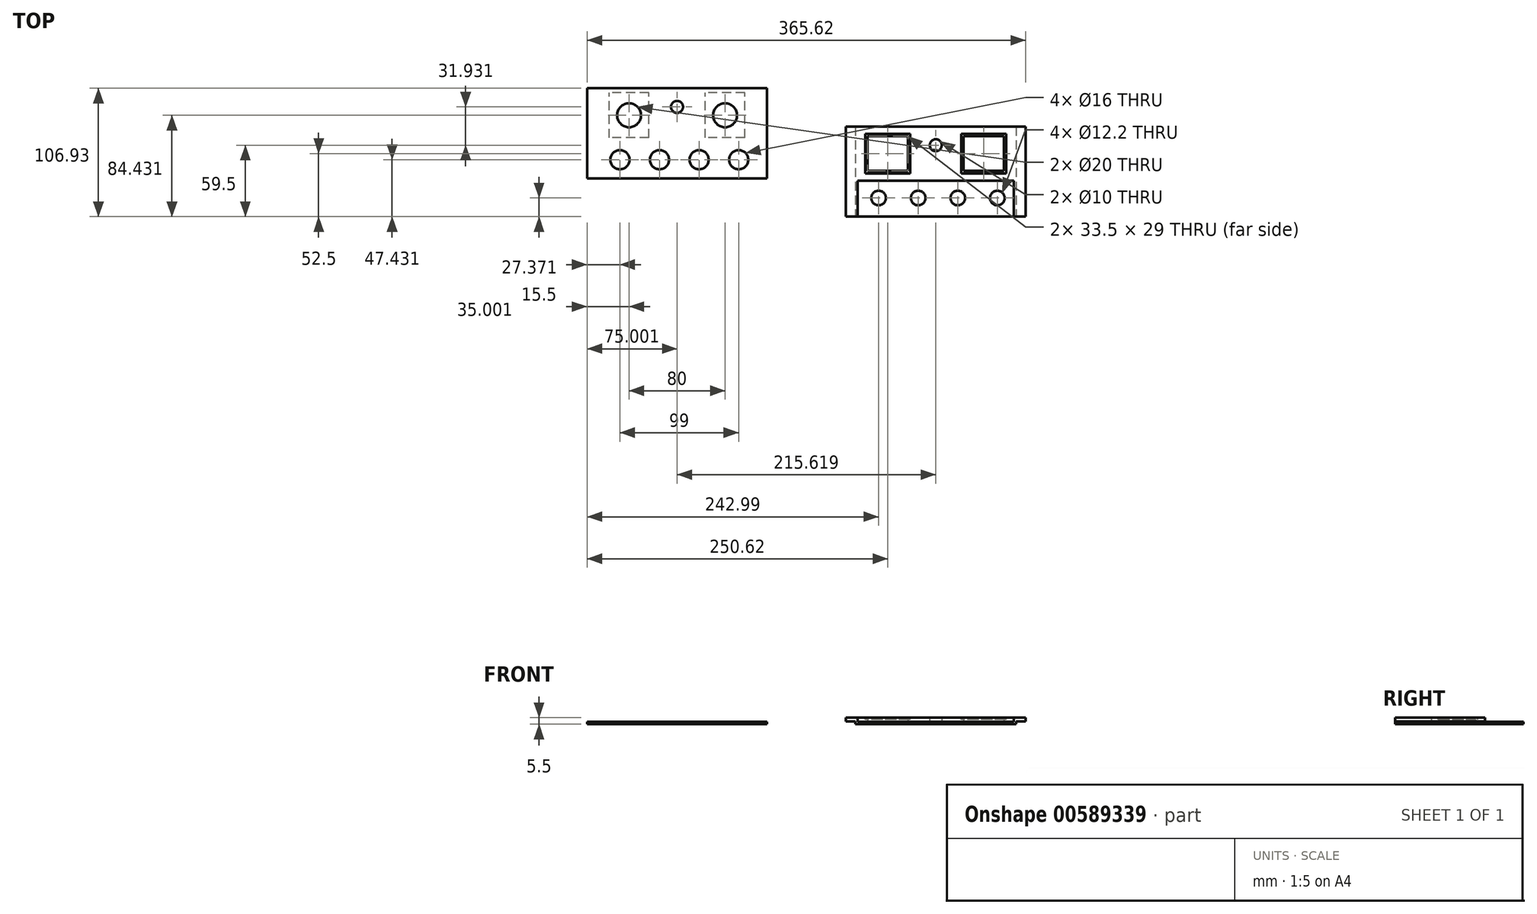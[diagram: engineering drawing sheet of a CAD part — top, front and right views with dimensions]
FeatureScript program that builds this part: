
annotation { "Feature Type Name" : "Feature", "Feature Type Description" : "" }
export const myFeature = defineFeature(function(context is Context, id is Id, definition is map)
    precondition{}
    {
        {
            var Q0;
            Q0=qCreatedBy(makeId("Top.planeOp"),FACE);
            var sketch = newSketch(context, id + "F0", { "sketchPlane" : qUnion([Q0])});
            skLineSegment(sketch, "E0.bottom", {"start": v(75, -37.5) * mm, "end": v(-75, -37.5) * mm});
            skLineSegment(sketch, "E0.top", {"start": v(75, 37.5) * mm, "end": v(-75, 37.5) * mm});
            skLineSegment(sketch, "E0.left", {"start": v(75, -37.5) * mm, "end": v(75, 37.5) * mm});
            skLineSegment(sketch, "E0.right", {"start": v(-75, -37.5) * mm, "end": v(-75, 37.5) * mm});
            skPoint(sketch, "E0.middle", {"position": v(0, 0) * mm});
            skCircle(sketch, "E1", {"center": v(0, 22) * mm, "radius": 5 * mm});
            skCircle(sketch, "E2", {"center": v(-47.63, -22) * mm, "radius": 6.1 * mm});
            skCircle(sketch, "E3.1.0.0", {"center": v(-14.63, -22) * mm, "radius": 6.1 * mm});
            skCircle(sketch, "E3.2.0.0", {"center": v(18.37, -22) * mm, "radius": 6.1 * mm});
            skCircle(sketch, "E3.3.0.0", {"center": v(51.37, -22) * mm, "radius": 6.1 * mm});
            skLineSegment(sketch, "E3.direction1", {"start": v(-47.63, -22) * mm, "end": v(-14.63, -22) * mm, "construction": true});
            skLineSegment(sketch, "E4.bottom", {"start": v(-75, 37.5) * mm, "end": v(-65, 37.5) * mm, "construction": true});
            skLineSegment(sketch, "E4.top", {"start": v(-75, -37.5) * mm, "end": v(-65, -37.5) * mm, "construction": true});
            skLineSegment(sketch, "E4.left", {"start": v(-75, 37.5) * mm, "end": v(-75, -37.5) * mm, "construction": true});
            skLineSegment(sketch, "E4.right", {"start": v(-65, 37.5) * mm, "end": v(-65, -37.5) * mm, "construction": true});
            skLineSegment(sketch, "E5.bottom", {"start": v(75, 37.5) * mm, "end": v(65, 37.5) * mm, "construction": true});
            skLineSegment(sketch, "E5.top", {"start": v(75, -37.5) * mm, "end": v(65, -37.5) * mm, "construction": true});
            skLineSegment(sketch, "E5.left", {"start": v(75, 37.5) * mm, "end": v(75, -37.5) * mm, "construction": true});
            skLineSegment(sketch, "E5.right", {"start": v(65, 37.5) * mm, "end": v(65, -37.5) * mm, "construction": true});
            skPoint(sketch, "E6.middle", {"position": v(-40, 15) * mm});
            skLineSegment(sketch, "E7.bottom", {"start": v(-23.25, 0.5) * mm, "end": v(-56.75, 0.5) * mm});
            skLineSegment(sketch, "E7.top", {"start": v(-23.25, 29.5) * mm, "end": v(-56.75, 29.5) * mm});
            skLineSegment(sketch, "E7.left", {"start": v(-23.25, 0.5) * mm, "end": v(-23.25, 29.5) * mm});
            skLineSegment(sketch, "E7.right", {"start": v(-56.75, 0.5) * mm, "end": v(-56.75, 29.5) * mm});
            skLineSegment(sketch, "E8.bottom", {"start": v(56.75, 0.5) * mm, "end": v(23.25, 0.5) * mm});
            skLineSegment(sketch, "E8.top", {"start": v(56.75, 29.5) * mm, "end": v(23.25, 29.5) * mm});
            skLineSegment(sketch, "E8.left", {"start": v(56.75, 0.5) * mm, "end": v(56.75, 29.5) * mm});
            skLineSegment(sketch, "E8.right", {"start": v(23.25, 0.5) * mm, "end": v(23.25, 29.5) * mm});
            skPoint(sketch, "E8.middle", {"position": v(40, 15) * mm});
            skPoint(sketch, "E9.centerSnap0", {"position": v(-70, 37.5) * mm});
            skCircle(sketch, "E10", {"center": v(-70, 25) * mm, "radius": 1.5 * mm});
            skCircle(sketch, "E11", {"center": v(-70, -25) * mm, "radius": 1.5 * mm});
            skCircle(sketch, "E12", {"center": v(70, 25) * mm, "radius": 1.5 * mm});
            skCircle(sketch, "E13", {"center": v(70, -25) * mm, "radius": 1.5 * mm});
            skSolve(sketch);
        }
        {
            var Q0;
            Q0=makeQuery(id+"F0.imprint","IMPRINT",FACE,{"disambiguationData":[TD([[makeQuery(id+"F0.imprint","IMPRINT",EDGE,{"derivedFrom":sQuery(id+"F0.wireOp",EDGE,"E0.bottom")}),-1.0]])]});
            var Q1;
            Q1=makeQuery(id+"F0.imprint","IMPRINT",FACE,{"disambiguationData":[TD([[makeQuery(id+"F0.imprint","IMPRINT",EDGE,{"derivedFrom":sQuery(id+"F0.wireOp",EDGE,"drD5jItb-HEpr-sxaA-TqkW-DfUxLCmm6Exs")}),-1.0]])]});
            extrude(context, id + "F1", {"entities" : qUnion([Q0, Q1]), "depth" : 2 * mm});
        }
        {
            var Q0;
            Q0=makeQuery(id+"F1.opExtrude","CAP_FACE",FACE,{"disambiguationData":[OSD([sQuery(id+"F0.wireOp",EDGE,"E0.bottom"),sQuery(id+"F0.wireOp",EDGE,"E0.top"),sQuery(id+"F0.wireOp",EDGE,"E0.left"),sQuery(id+"F0.wireOp",EDGE,"E0.right"),sQuery(id+"F0.wireOp",EDGE,"drD5jItb-HEpr-sxaA-TqkW-DfUxLCmm6Exs"),sQuery(id+"F0.wireOp",EDGE,"oSn99fef-1uPw-k3Do-L9e6-x1k65rtnndGm"),sQuery(id+"F0.wireOp",EDGE,"E1"),sQuery(id+"F0.wireOp",EDGE,"E2"),sQuery(id+"F0.wireOp",EDGE,"E3.1.0.0"),sQuery(id+"F0.wireOp",EDGE,"E3.2.0.0"),sQuery(id+"F0.wireOp",EDGE,"E3.3.0.0")])],"isStart":false});
            var sketch = newSketch(context, id + "F2", { "sketchPlane" : qUnion([Q0])});
            skLineSegment(sketch, "E14.bottom", {"start": v(-75, 37.5) * mm, "end": v(-65, 37.5) * mm});
            skLineSegment(sketch, "E14.top", {"start": v(-75, -37.5) * mm, "end": v(-65, -37.5) * mm});
            skLineSegment(sketch, "E14.left", {"start": v(-75, 37.5) * mm, "end": v(-75, -37.5) * mm});
            skLineSegment(sketch, "E14.right", {"start": v(-65, 37.5) * mm, "end": v(-65, -37.5) * mm});
            skLineSegment(sketch, "E15.bottom", {"start": v(75, -37.5) * mm, "end": v(65, -37.5) * mm});
            skLineSegment(sketch, "E15.top", {"start": v(75, 37.5) * mm, "end": v(65, 37.5) * mm});
            skLineSegment(sketch, "E15.left", {"start": v(75, -37.5) * mm, "end": v(75, 37.5) * mm});
            skLineSegment(sketch, "E15.right", {"start": v(65, -37.5) * mm, "end": v(65, 37.5) * mm});
            skSolve(sketch);
        }
        {
            var Q0;
            Q0=qSketchRegion(id+"F2",true);
            extrude(context, id + "F3", {"entities" : qUnion([Q0]), "operationType" : NewBodyOperationType.ADD, "depth" : 3.5 * mm});
        }
        {
            var Q0;
            Q0=makeQuery(id+"F3.boolean.opBoolean","MERGE",FACE,{"derivedFrom":[makeQuery(id+"F1.opExtrude","SWEPT_FACE",FACE,{"disambiguationData":[OSD([sQuery(id+"F0.wireOp",EDGE,"E0.bottom")])]}),makeQuery(id+"F3.opExtrude","SWEPT_FACE",FACE,{"disambiguationData":[OSD([sQuery(id+"F2.wireOp",EDGE,"E14.top")])]}),makeQuery(id+"F3.opExtrude","SWEPT_FACE",FACE,{"disambiguationData":[OSD([sQuery(id+"F2.wireOp",EDGE,"E15.bottom")])]})]});
            var sketch = newSketch(context, id + "F4", { "sketchPlane" : qUnion([Q0])});
            skLineSegment(sketch, "E16.bottom", {"start": v(-75, 0) * mm, "end": v(-67, 0) * mm});
            skLineSegment(sketch, "E16.top", {"start": v(-75, 2.5) * mm, "end": v(-67, 2.5) * mm});
            skLineSegment(sketch, "E16.left", {"start": v(-75, 0) * mm, "end": v(-75, 2.5) * mm});
            skLineSegment(sketch, "E16.right", {"start": v(-67, 0) * mm, "end": v(-67, 2.5) * mm});
            skLineSegment(sketch, "E17.bottom", {"start": v(75, 0) * mm, "end": v(67, 0) * mm});
            skLineSegment(sketch, "E17.top", {"start": v(75, 2.5) * mm, "end": v(67, 2.5) * mm});
            skLineSegment(sketch, "E17.left", {"start": v(75, 0) * mm, "end": v(75, 2.5) * mm});
            skLineSegment(sketch, "E17.right", {"start": v(67, 0) * mm, "end": v(67, 2.5) * mm});
            skSolve(sketch);
        }
        {
            var Q0;
            Q0=qSketchRegion(id+"F4",true);
            extrude(context, id + "F5", {"entities" : qUnion([Q0]), "operationType" : NewBodyOperationType.REMOVE, "oppositeDirection" : true, "depth" : 80 * mm});
        }
        {
            var Q0;
            Q0=makeQuery(id+"F1.opExtrude","CAP_FACE",FACE,{"disambiguationData":[OSD([sQuery(id+"F0.wireOp",EDGE,"E0.bottom"),sQuery(id+"F0.wireOp",EDGE,"E0.top"),sQuery(id+"F0.wireOp",EDGE,"E0.left"),sQuery(id+"F0.wireOp",EDGE,"E0.right"),sQuery(id+"F0.wireOp",EDGE,"drD5jItb-HEpr-sxaA-TqkW-DfUxLCmm6Exs"),sQuery(id+"F0.wireOp",EDGE,"oSn99fef-1uPw-k3Do-L9e6-x1k65rtnndGm"),sQuery(id+"F0.wireOp",EDGE,"E1"),sQuery(id+"F0.wireOp",EDGE,"E2"),sQuery(id+"F0.wireOp",EDGE,"E3.1.0.0"),sQuery(id+"F0.wireOp",EDGE,"E3.2.0.0"),sQuery(id+"F0.wireOp",EDGE,"E3.3.0.0")])],"isStart":false});
            var sketch = newSketch(context, id + "F6", { "sketchPlane" : qUnion([Q0])});
            skLineSegment(sketch, "E18.bottom", {"start": v(-65, 37.5) * mm, "end": v(65, 37.5) * mm});
            skLineSegment(sketch, "E18.top", {"start": v(-65, -7.5) * mm, "end": v(65, -7.5) * mm});
            skLineSegment(sketch, "E18.left", {"start": v(-65, 37.5) * mm, "end": v(-65, -7.5) * mm});
            skLineSegment(sketch, "E18.right", {"start": v(65, 37.5) * mm, "end": v(65, -7.5) * mm});
            skCircle(sketch, "E19", {"center": v(0, 22) * mm, "radius": 5 * mm});
            skLineSegment(sketch, "E20.bottom", {"start": v(-23.25, 0.5) * mm, "end": v(-56.75, 0.5) * mm});
            skLineSegment(sketch, "E20.top", {"start": v(-23.25, 29.5) * mm, "end": v(-56.75, 29.5) * mm});
            skLineSegment(sketch, "E20.left", {"start": v(-23.25, 0.5) * mm, "end": v(-23.25, 29.5) * mm});
            skLineSegment(sketch, "E20.right", {"start": v(-56.75, 0.5) * mm, "end": v(-56.75, 29.5) * mm});
            skPoint(sketch, "E20.middle", {"position": v(-40, 15) * mm});
            skLineSegment(sketch, "E21.bottom", {"start": v(56.75, 0.5) * mm, "end": v(23.25, 0.5) * mm});
            skLineSegment(sketch, "E21.top", {"start": v(56.75, 29.5) * mm, "end": v(23.25, 29.5) * mm});
            skLineSegment(sketch, "E21.left", {"start": v(56.75, 0.5) * mm, "end": v(56.75, 29.5) * mm});
            skLineSegment(sketch, "E21.right", {"start": v(23.25, 0.5) * mm, "end": v(23.25, 29.5) * mm});
            skPoint(sketch, "E21.middle", {"position": v(40, 15) * mm});
            skSolve(sketch);
        }
        {
            var Q0;
            Q0=qSketchRegion(id+"F6",true);
            extrude(context, id + "F7", {"entities" : qUnion([Q0]), "operationType" : NewBodyOperationType.ADD, "depth" : 3.5 * mm});
        }
        {
            var Q0;
            Q0=makeQuery(id+"F7.boolean.opBoolean","MERGE",FACE,{"derivedFrom":[makeQuery(id+"F3.opExtrude","CAP_FACE",FACE,{"disambiguationData":[OSD([sQuery(id+"F2.wireOp",EDGE,"E14.bottom"),sQuery(id+"F2.wireOp",EDGE,"E14.top"),sQuery(id+"F2.wireOp",EDGE,"E14.left"),sQuery(id+"F2.wireOp",EDGE,"E14.right")])],"isStart":false}),makeQuery(id+"F3.opExtrude","CAP_FACE",FACE,{"disambiguationData":[OSD([sQuery(id+"F2.wireOp",EDGE,"E15.bottom"),sQuery(id+"F2.wireOp",EDGE,"E15.top"),sQuery(id+"F2.wireOp",EDGE,"E15.left"),sQuery(id+"F2.wireOp",EDGE,"E15.right")])],"isStart":false}),makeQuery(id+"F7.opExtrude","CAP_FACE",FACE,{"disambiguationData":[OSD([sQuery(id+"F6.wireOp",EDGE,"E18.bottom"),sQuery(id+"F6.wireOp",EDGE,"E18.top"),sQuery(id+"F6.wireOp",EDGE,"E18.left"),sQuery(id+"F6.wireOp",EDGE,"E18.right"),sQuery(id+"F6.wireOp",EDGE,"H2Zb9yD0-p2Z7-Kh5e-a6hj-aLUdcpXocAIw"),sQuery(id+"F6.wireOp",EDGE,"7ZJ2aJG6-LJXW-fwXF-v4kC-qdLRGwjfnqPK"),sQuery(id+"F6.wireOp",EDGE,"E19")])],"isStart":false})]});
            var sketch = newSketch(context, id + "F8", { "sketchPlane" : qUnion([Q0])});
            skLineSegment(sketch, "E22.bottom", {"start": v(-21.25, -1.5) * mm, "end": v(-58.75, -1.5) * mm});
            skLineSegment(sketch, "E22.top", {"start": v(-21.25, 31.5) * mm, "end": v(-58.75, 31.5) * mm});
            skLineSegment(sketch, "E22.left", {"start": v(-21.25, -1.5) * mm, "end": v(-21.25, 31.5) * mm});
            skLineSegment(sketch, "E22.right", {"start": v(-58.75, -1.5) * mm, "end": v(-58.75, 31.5) * mm});
            skPoint(sketch, "E22.middle", {"position": v(-40, 15) * mm});
            skLineSegment(sketch, "E23.bottom", {"start": v(58.75, -1.5) * mm, "end": v(21.25, -1.5) * mm});
            skLineSegment(sketch, "E23.top", {"start": v(58.75, 31.5) * mm, "end": v(21.25, 31.5) * mm});
            skLineSegment(sketch, "E23.left", {"start": v(58.75, -1.5) * mm, "end": v(58.75, 31.5) * mm});
            skLineSegment(sketch, "E23.right", {"start": v(21.25, -1.5) * mm, "end": v(21.25, 31.5) * mm});
            skPoint(sketch, "E23.middle", {"position": v(40, 15) * mm});
            skSolve(sketch);
        }
        {
            var Q0;
            Q0=makeQuery(id+"F8.imprint","IMPRINT",FACE,{"disambiguationData":[TD([[makeQuery(id+"F8.imprint","IMPRINT",EDGE,{"derivedFrom":sQuery(id+"F8.wireOp",EDGE,"E22.bottom")}),-1.0]])]});
            var Q1;
            Q1=makeQuery(id+"F8.imprint","IMPRINT",FACE,{"disambiguationData":[TD([[makeQuery(id+"F8.imprint","IMPRINT",EDGE,{"derivedFrom":sQuery(id+"F8.wireOp",EDGE,"E23.bottom")}),-1.0]])]});
            extrude(context, id + "F9", {"entities" : qUnion([Q0, Q1]), "operationType" : NewBodyOperationType.REMOVE, "oppositeDirection" : true, "depth" : 1.5 * mm});
        }
        {
            var Q0;
            Q0=qCreatedBy(makeId("Top.planeOp"),FACE);
            var sketch = newSketch(context, id + "F10", { "sketchPlane" : qUnion([Q0])});
            skLineSegment(sketch, "E24.bottom", {"start": v(-140.62, -5.57) * mm, "end": v(-290.62, -5.57) * mm});
            skLineSegment(sketch, "E24.top", {"start": v(-140.62, 69.43) * mm, "end": v(-290.62, 69.43) * mm});
            skLineSegment(sketch, "E24.left", {"start": v(-140.62, -5.57) * mm, "end": v(-140.62, 69.43) * mm});
            skLineSegment(sketch, "E24.right", {"start": v(-290.62, -5.57) * mm, "end": v(-290.62, 69.43) * mm});
            skPoint(sketch, "E24.middle", {"position": v(-215.62, 31.93) * mm});
            skCircle(sketch, "E25", {"center": v(-215.62, 53.93) * mm, "radius": 5 * mm});
            skCircle(sketch, "E26", {"center": v(-263.25, 9.93) * mm, "radius": 8 * mm});
            skCircle(sketch, "E27.1.0.0", {"center": v(-230.25, 9.93) * mm, "radius": 8 * mm});
            skCircle(sketch, "E27.2.0.0", {"center": v(-197.25, 9.93) * mm, "radius": 8 * mm});
            skCircle(sketch, "E27.3.0.0", {"center": v(-164.25, 9.93) * mm, "radius": 8 * mm});
            skLineSegment(sketch, "E27.direction1", {"start": v(-263.25, 9.93) * mm, "end": v(-230.25, 9.93) * mm, "construction": true});
            skLineSegment(sketch, "E28.bottom", {"start": v(-290.62, 69.43) * mm, "end": v(-280.62, 69.43) * mm, "construction": true});
            skLineSegment(sketch, "E28.top", {"start": v(-290.62, -5.57) * mm, "end": v(-280.62, -5.57) * mm, "construction": true});
            skLineSegment(sketch, "E28.left", {"start": v(-290.62, 69.43) * mm, "end": v(-290.62, -5.57) * mm, "construction": true});
            skLineSegment(sketch, "E28.right", {"start": v(-280.62, 69.43) * mm, "end": v(-280.62, -5.57) * mm, "construction": true});
            skLineSegment(sketch, "E29.bottom", {"start": v(-140.62, 69.43) * mm, "end": v(-150.62, 69.43) * mm, "construction": true});
            skLineSegment(sketch, "E29.top", {"start": v(-140.62, -5.57) * mm, "end": v(-150.62, -5.57) * mm, "construction": true});
            skLineSegment(sketch, "E29.left", {"start": v(-140.62, 69.43) * mm, "end": v(-140.62, -5.57) * mm, "construction": true});
            skLineSegment(sketch, "E29.right", {"start": v(-150.62, 69.43) * mm, "end": v(-150.62, -5.57) * mm, "construction": true});
            skPoint(sketch, "E30.middle", {"position": v(-255.62, 46.93) * mm});
            skPoint(sketch, "E31.middle", {"position": v(-175.62, 46.93) * mm});
            skCircle(sketch, "E32", {"center": v(-255.62, 46.93) * mm, "radius": 10 * mm});
            skCircle(sketch, "E33", {"center": v(-175.62, 46.93) * mm, "radius": 10 * mm});
            skLineSegment(sketch, "E34.bottom", {"start": v(-236.87, 30.43) * mm, "end": v(-274.37, 30.43) * mm, "construction": true});
            skLineSegment(sketch, "E34.top", {"start": v(-236.87, 63.43) * mm, "end": v(-274.37, 63.43) * mm, "construction": true});
            skLineSegment(sketch, "E34.left", {"start": v(-236.87, 30.43) * mm, "end": v(-236.87, 63.43) * mm, "construction": true});
            skLineSegment(sketch, "E34.right", {"start": v(-274.37, 30.43) * mm, "end": v(-274.37, 63.43) * mm, "construction": true});
            skLineSegment(sketch, "E35.bottom", {"start": v(-156.87, 30.43) * mm, "end": v(-194.37, 30.43) * mm, "construction": true});
            skLineSegment(sketch, "E35.top", {"start": v(-156.87, 63.43) * mm, "end": v(-194.37, 63.43) * mm, "construction": true});
            skLineSegment(sketch, "E35.left", {"start": v(-156.87, 30.43) * mm, "end": v(-156.87, 63.43) * mm, "construction": true});
            skLineSegment(sketch, "E35.right", {"start": v(-194.37, 30.43) * mm, "end": v(-194.37, 63.43) * mm, "construction": true});
            skSolve(sketch);
        }
        {
            var Q0;
            Q0=makeQuery(id+"F10.imprint","IMPRINT",FACE,{"disambiguationData":[TD([[makeQuery(id+"F10.imprint","IMPRINT",EDGE,{"derivedFrom":sQuery(id+"F10.wireOp",EDGE,"E24.bottom")}),-1.0]])]});
            extrude(context, id + "F11", {"entities" : qUnion([Q0]), "depth" : 2 * mm});
        }
        {
            var Q0;
            Q0=makeQuery(id+"F11.opExtrude","CAP_FACE",FACE,{"disambiguationData":[OSD([sQuery(id+"F10.wireOp",EDGE,"E24.bottom"),sQuery(id+"F10.wireOp",EDGE,"E24.top"),sQuery(id+"F10.wireOp",EDGE,"E24.left"),sQuery(id+"F10.wireOp",EDGE,"E24.right"),sQuery(id+"F10.wireOp",EDGE,"E25"),sQuery(id+"F10.wireOp",EDGE,"E26"),sQuery(id+"F10.wireOp",EDGE,"E27.1.0.0"),sQuery(id+"F10.wireOp",EDGE,"E27.2.0.0"),sQuery(id+"F10.wireOp",EDGE,"E27.3.0.0"),sQuery(id+"F10.wireOp",EDGE,"E32"),sQuery(id+"F10.wireOp",EDGE,"E33")])],"isStart":true});
            var sketch = newSketch(context, id + "F12", { "sketchPlane" : qUnion([Q0])});
            skLineSegment(sketch, "E36.bottom", {"start": v(-239.12, -28.18) * mm, "end": v(-272.12, -28.18) * mm});
            skLineSegment(sketch, "E36.top", {"start": v(-239.12, -65.68) * mm, "end": v(-272.12, -65.68) * mm});
            skLineSegment(sketch, "E36.left", {"start": v(-239.12, -28.18) * mm, "end": v(-239.12, -65.68) * mm});
            skLineSegment(sketch, "E36.right", {"start": v(-272.12, -28.18) * mm, "end": v(-272.12, -65.68) * mm});
            skPoint(sketch, "E36.middle", {"position": v(-255.62, -46.93) * mm});
            skLineSegment(sketch, "E37.bottom", {"start": v(-159.12, -28.18) * mm, "end": v(-192.12, -28.18) * mm});
            skLineSegment(sketch, "E37.top", {"start": v(-159.12, -65.68) * mm, "end": v(-192.12, -65.68) * mm});
            skLineSegment(sketch, "E37.left", {"start": v(-159.12, -28.18) * mm, "end": v(-159.12, -65.68) * mm});
            skLineSegment(sketch, "E37.right", {"start": v(-192.12, -28.18) * mm, "end": v(-192.12, -65.68) * mm});
            skPoint(sketch, "E37.middle", {"position": v(-175.62, -46.93) * mm});
            skSolve(sketch);
        }
        {
            var Q0;
            Q0=qSketchRegion(id+"F12",true);
            extrude(context, id + "F13", {"entities" : qUnion([Q0]), "operationType" : NewBodyOperationType.REMOVE, "oppositeDirection" : true, "depth" : 1 * mm});
        }
    });
